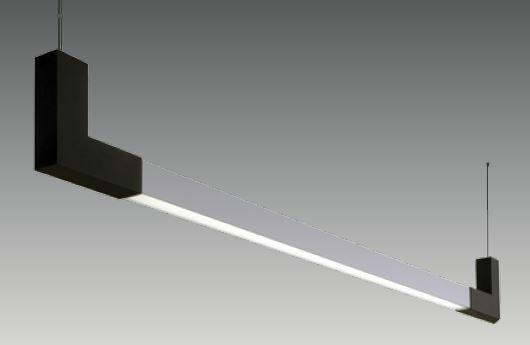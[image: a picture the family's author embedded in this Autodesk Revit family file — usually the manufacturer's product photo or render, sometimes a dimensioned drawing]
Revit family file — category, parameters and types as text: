
# Revit family: S 1500 PLU
name_source: partatom
category: Lighting Fixtures
revit_build: Autodesk Revit 2017 (Build: 20160225_1515(x64)
units: mm (PartAtom-declared; Revit-internal decimal feet)

## family parameters
Cut with Voids When Loaded = No
Host = Face
Light Source = Yes
Part Type = Normal
Room Calculation Point = No
Round Connector Dimension = Use Diameter
Shared = No

## types (2) — shared parameters
Apparent Load = 44 VA
Color Filter = 16777215
Default Elevation = 1219 mm
Dimming Lamp Color Temperature Shift = <None>
Emit Shape Visible in Rendering = Yes
Emit from Rectangle Length = 40 mm  [stored 0.131234 ft]
Emit from Rectangle Width = 1135 mm  [stored 3.72375 ft]
Light Source Symbol Size = 610 mm
Manufacturer = ARLIGHT
Type Image = S 1500 PLU.JPG
Wattage Comments = 44W

## type names (no varying parameters)
- SPLU.1500.44.30
- SPLU.1500.44.40

note: [stored X ft] marks values corroborated as IEEE doubles in the binary element streams (Revit-internal decimal feet)

## geometry (parser evidence)
native form markers: Sweep x2
no freeform markers — native parametric forms only
